# Revit family: Boiler-Gas-Weil-McLain-SVF_500-600
name_source: partatom
category: Mechanical Equipment
units: mm (PartAtom-declared; Revit-internal decimal feet)

## family parameters
Always vertical = Yes
Cut with Voids When Loaded = No
OmniClass Number = 23.75.10.11.14
OmniClass Title = Hot Water Heat Generators
Part Type = Normal
Room Calculation Point = No
Round Connector Dimension = Use Diameter
Shared = No
Work Plane-Based = Yes

## types (2) — shared parameters
Assembly Code = D3020100
Boiler Return Water Diameter = 2"
Boiler Supply Water Diameter = 2"
Condensate Drain Connection Diameter = 1"
CondensateCL = 0' - 4"
CondensateLocate = 0' - 10 1/4"
Dead Weight = 472
Default Elevation = 0' - 0"
Description = Weil-McLain Commercial NG Gas Boiler - SVF 500 as Specified
Flue Diameter = 1"
Flue Inset = 1' - 0 7/32"
Flue Locate = 6' - 5 9/16"
FlueHolderDia = 0' - 2 3/4"
Frame Accent Material = Plastic - WeilMcLain - Black
Frame Finish = Metal - WeilMcLain - Gray
Frequency = 60 Hz
Fuel Type = Natural Gas
Full Load Current = 23 A
Gas Connection Diameter = 1"
Gas Connection Type = Female NPT
Height = 4' - 1 29/32"
Keynote = 23 52 00
Length = 3' - 3 1/32"
Manufacturer = Weil-McLain
Net AHRI MBH = 616.0 Btu/h
Number of Poles = 1
Operating Temperature = 40 - 120 F
Operating Weight = 500
Phase = 1
Product Page URL = https://www.weil-mclain.com
Screen Material = Plastic - WeilMcLain - Blue
Standards Conformance = ASME  ;  AHRI  ;  CSA
Supply Air Connection Diameter = 4"
Tank Capacity = 12 gal
Thermal Efficiency = 97.7
Total Heating Capacity = 708.0 Btu/h
Type Comments = No Side Clearance. Side-by-Side install capable.
URL = https://www.weil-mclain.com
Version = 2020 - v1.0b
Voltage = 120 V
Water Connection Type = Class 150 ASME Flange
Width = 2' - 0 29/32"

## per-type parameters (varying)
| type | Model | Product Documentation Link | Product Name | Warranty URL |
| SVP 500 | SVF 500 | https://www.weil-mclain.com | SVF 500 | https://www.weil-mclain.com |
| SVP 600 | SVF 600 |  | SVF 600 |  |

## geometry (parser evidence)
native form markers: Sweep x1
no freeform markers — native parametric forms only
